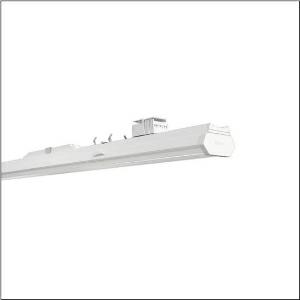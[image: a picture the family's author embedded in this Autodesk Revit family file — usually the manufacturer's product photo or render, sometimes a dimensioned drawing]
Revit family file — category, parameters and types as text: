
# Revit family: licross_21_protected_mo_52td1bvn48xg
name_source: partatom
category: Lighting Fixtures
units: mm (PartAtom-declared; Revit-internal decimal feet)

## family parameters
Cut with Voids When Loaded = No
Host = Face
Light Source = No
Part Type = Normal
Room Calculation Point = No
Round Connector Dimension = Use Diameter
Shared = No

## types (1)
- --- (1 x LED, 8000 lm, 48.3 W, 4000K)
    Apparent Load = 48 VA
    CIE Flux Codes = 54 82 95 97 100
    Color Rendering = 80
    Color Temperature = 4000K
    Default Elevation = 1800 mm
    Description = Licross 21 Protected MO, luminaire insert, of sheet steel, galvanised, coil coated, white, length: 1.500mm, width: 90mm, height: 101mm, LED rated luminous flux: 8.000lm, light colour: 840, SDCM (Standard Deviation of Colour Matching)MacAdam ≤ 3 SDCM (initial), control gear: DALI 2, CLO, with plug, 5-pole, with phase selection, mains connection: 220..240V, AC, 50/60Hz, start of lifetime: 48W, end of service life: 58W, internal wiring halogen-free, primary optical cover: cover, of PMMA, light emission: direct distribution, primary light characteristic: symmetric, protection rating (complete): IP54, insulation class (complete): insulation class I (protective earthing), certification: CE, ENEC, VDE, UKCA, protection symbol: D if used in an environment with non-conductive dust loads with corresponding accessories, impact resistance: IK06, permissible ambient temperature for indoor applications: -25..+40°C, corresponds to IFS (International Featured Standards) requirements for safety and quality in the food industry, reducing of maximum allowable ambient temperature of 5°C with ceiling mounting, LABS conformity tested according to VDMA 24364:2018-05, The light source and the operating device comply with the requirements of the Ecodesign Regulation (EU) 2019/2020 and are replaceable in accordance with this regulation, packaging unit: 1 piece
    Height = 92 mm
    Lamp = 1 x LED
    Lamp Light Flux = 8000 lm
    Lamp Power = 48.3 W
    Lamp count = 1
    Length = 1500 mm
    Luminous efficacy = 166 lm/W
    Manufacturer = Siteco
    ModVariant = No
    Model = 52TD1BVN48XG
    Mounting Place = Ceiling
    Mounting Type = Pendant
    Number of Poles = 1
    OnlyDefault = Yes
    Power Factor = 1
    Product Name = Licross 21 Protected MO
    Product group = luminaire insert | ceiling pendant
    ProductGroupID = 901
    Protection Class = Protection class I
    Protection Degree = IP 54
    RLX_Detail_Level = 1
    RLX_Emergency_Light_Flux = 0 lm
    RLX_Emergency_Type = 0
    RLX_Emergency_Type_DB = No
    RlxData = <blob elided: 24529 chars, md5=d7d6df4b>
    Socket = socket
    Standby Power = 0 W
    System Light Flux = 8000 lm
    System Power = 48 W
    Type Comments = factory setting: luminous flux: 100 % | dim-lin: 254 | 326 mA
    Type Image = l_1256148.jpg
    URL = http://relux.com
    VarID = @adj_087909
    Voltage = 0 V
    Weight = 0.00 kg
    Width = 88 mm

## geometry (parser evidence)
native form markers: Blend x4, Sweep x11
no freeform markers — native parametric forms only
